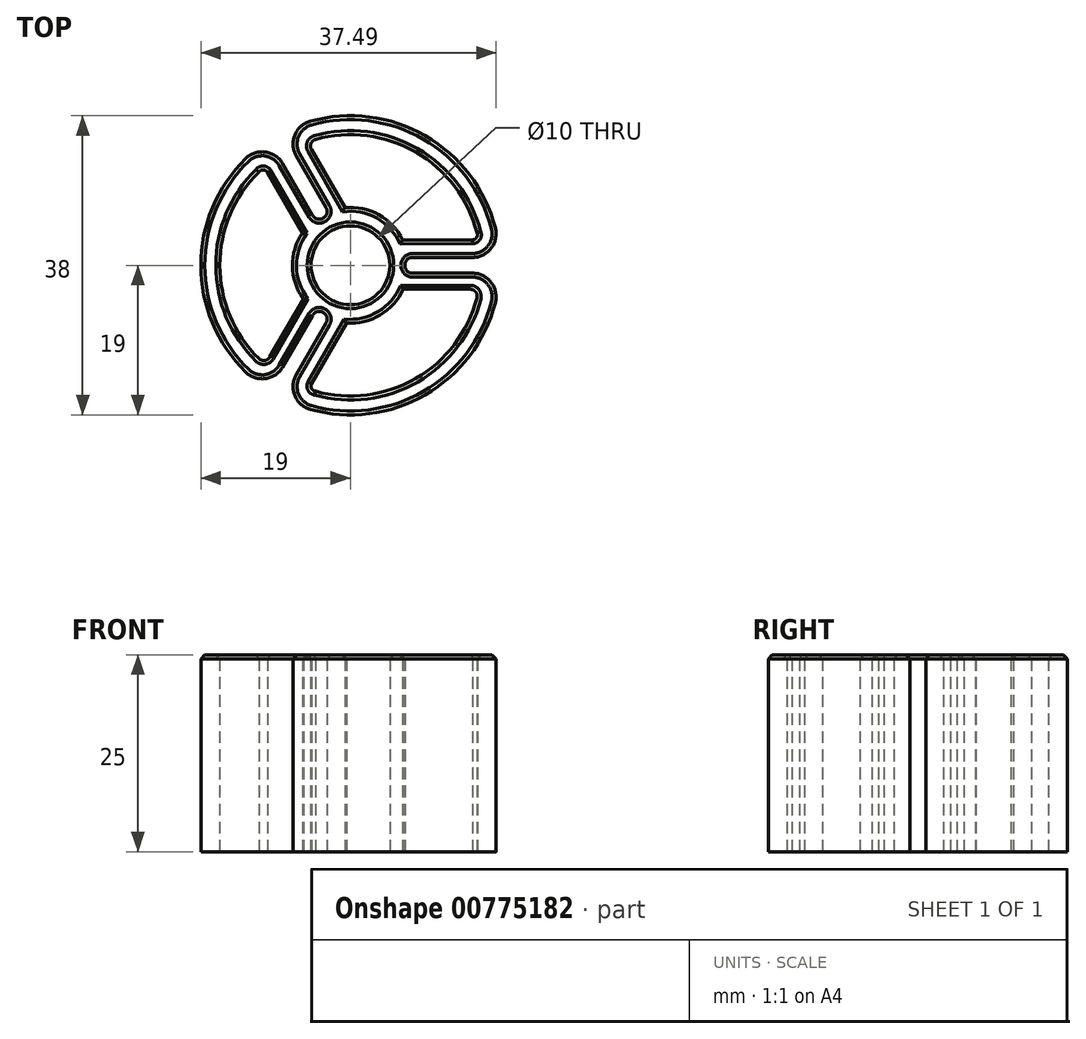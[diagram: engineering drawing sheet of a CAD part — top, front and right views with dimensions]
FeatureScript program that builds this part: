
annotation { "Feature Type Name" : "Feature", "Feature Type Description" : "" }
export const myFeature = defineFeature(function(context is Context, id is Id, definition is map)
    precondition{}
    {
        {
            var Q0;
            Q0=qCreatedBy(makeId("Top.planeOp"),FACE);
            var sketch = newSketch(context, id + "F0", { "sketchPlane" : qUnion([Q0])});
            skArc(sketch, "E0", {"start": v(-4.75, 18.4) * mm, "mid": v(-4.92, 18.35) * mm, "end": v(-5.08, 18.3) * mm});
            skArc(sketch, "E1.0", {"start": v(-4.25, 16.46) * mm, "mid": v(-4.4, 16.42) * mm, "end": v(-4.55, 16.38) * mm});
            skLineSegment(sketch, "E2", {"start": v(0, 19) * mm, "end": v(0, 40.88) * mm});
            skCircle(sketch, "E3.converted", {"center": v(0, 0) * mm, "radius": 5 * mm});
            skArc(sketch, "E4.converted", {"start": v(6.37, 2.82) * mm, "mid": v(3.4, 6.08) * mm, "end": v(-0.93, 6.9) * mm});
            skPoint(sketch, "E5.orphan", {"position": v(-3, 6.32) * mm});
            skLineSegment(sketch, "E6.3.0", {"start": v(15.5, 2.83) * mm, "end": v(10.9, 2.83) * mm});
            skArc(sketch, "E6.3.2", {"start": v(7.9, 1) * mm, "mid": v(6.9, 0) * mm, "end": v(7.9, -1) * mm});
            skLineSegment(sketch, "E6.3.3", {"start": v(12, 1) * mm, "end": v(15.5, 1) * mm});
            skLineSegment(sketch, "E6.3.4", {"start": v(15.22, -2.65) * mm, "end": v(10.83, -2.65) * mm});
            skArc(sketch, "E6.3.5", {"start": v(15.5, 1) * mm, "mid": v(17.86, 2.16) * mm, "end": v(18.4, 4.75) * mm});
            skLineSegment(sketch, "E6.3.6", {"start": v(12, -1) * mm, "end": v(15.5, -1) * mm});
            skPoint(sketch, "E6.3.7", {"position": v(16.73, 3) * mm});
            skArc(sketch, "E6.3.8", {"start": v(18.4, -4.75) * mm, "mid": v(17.86, -2.16) * mm, "end": v(15.5, -1) * mm});
            skPoint(sketch, "E6.3.9", {"position": v(16.73, -3) * mm});
            skArc(sketch, "E6.3.10", {"start": v(15.5, 2.83) * mm, "mid": v(16.35, 3.3) * mm, "end": v(16.46, 4.26) * mm});
            skArc(sketch, "E6.3.11", {"start": v(16.46, -4.25) * mm, "mid": v(16.23, -3.14) * mm, "end": v(15.22, -2.65) * mm});
            skLineSegment(sketch, "E6.3.12", {"start": v(12, 1) * mm, "end": v(7.9, 1) * mm});
            skLineSegment(sketch, "E6.3.13", {"start": v(12, -1) * mm, "end": v(7.9, -1) * mm});
            skArc(sketch, "E7.trimOffspring", {"start": v(16.46, 4.26) * mm, "mid": v(8.63, 14.65) * mm, "end": v(-4.25, 16.46) * mm});
            skArc(sketch, "E8.trimOffspring", {"start": v(18.4, 4.75) * mm, "mid": v(9.65, 16.37) * mm, "end": v(-4.75, 18.4) * mm});
            skArc(sketch, "E9.trimOffspring", {"start": v(-4.75, -18.4) * mm, "mid": v(9.65, -16.37) * mm, "end": v(18.4, -4.75) * mm});
            skArc(sketch, "E10.trimOffspring", {"start": v(-4.25, -16.46) * mm, "mid": v(8.63, -14.64) * mm, "end": v(16.46, -4.25) * mm});
            skArc(sketch, "E11.trimOffspring", {"start": v(-18.4, -4.75) * mm, "mid": v(-16.45, -9.5) * mm, "end": v(-13.31, -13.56) * mm});
            skArc(sketch, "E12.trimOffspring", {"start": v(-16.46, -4.25) * mm, "mid": v(-14.72, -8.5) * mm, "end": v(-11.91, -12.13) * mm});
            skLineSegment(sketch, "E13", {"start": v(10.9, 2.83) * mm, "end": v(6.37, 2.82) * mm});
            skLineSegment(sketch, "E14", {"start": v(10.83, -2.65) * mm, "end": v(6.44, -2.65) * mm});
            skArc(sketch, "E15.1.0", {"start": v(-8.61, 12.92) * mm, "mid": v(-10.8, 14.39) * mm, "end": v(-13.31, 13.56) * mm});
            skArc(sketch, "E15.1.1", {"start": v(-4.82, 6.35) * mm, "mid": v(-3.45, 5.98) * mm, "end": v(-3.09, 7.35) * mm});
            skArc(sketch, "E15.1.2", {"start": v(-5.08, 18.3) * mm, "mid": v(-7.06, 16.55) * mm, "end": v(-6.88, 13.92) * mm});
            skLineSegment(sketch, "E15.1.3", {"start": v(-5.32, 14.5) * mm, "end": v(-3.12, 10.7) * mm});
            skPoint(sketch, "E15.1.4", {"position": v(-10.96, 13) * mm});
            skLineSegment(sketch, "E15.1.5", {"start": v(-6.87, 9.9) * mm, "end": v(-4.82, 6.35) * mm});
            skLineSegment(sketch, "E15.1.6", {"start": v(-3.12, 10.7) * mm, "end": v(-0.93, 6.9) * mm});
            skLineSegment(sketch, "E15.1.7", {"start": v(-5.13, 10.9) * mm, "end": v(-3.09, 7.35) * mm});
            skLineSegment(sketch, "E15.1.8", {"start": v(-6.87, 9.9) * mm, "end": v(-8.61, 12.92) * mm});
            skLineSegment(sketch, "E15.1.9", {"start": v(-5.13, 10.9) * mm, "end": v(-6.88, 13.92) * mm});
            skLineSegment(sketch, "E15.1.10", {"start": v(-7.9, 8.03) * mm, "end": v(-5.63, 4.1) * mm});
            skLineSegment(sketch, "E15.1.11", {"start": v(-10.2, 12) * mm, "end": v(-7.9, 8.03) * mm});
            skPoint(sketch, "E15.1.12", {"position": v(-5.77, 16) * mm});
            skArc(sketch, "E15.1.13", {"start": v(-10.2, 12) * mm, "mid": v(-11.03, 12.5) * mm, "end": v(-11.92, 12.12) * mm});
            skArc(sketch, "E15.1.14", {"start": v(-4.55, 16.38) * mm, "mid": v(-5.4, 15.63) * mm, "end": v(-5.32, 14.5) * mm});
            skArc(sketch, "E15.2.0", {"start": v(-6.88, -13.92) * mm, "mid": v(-7.06, -16.55) * mm, "end": v(-5.08, -18.3) * mm});
            skArc(sketch, "E15.2.1", {"start": v(-3.09, -7.35) * mm, "mid": v(-3.45, -5.98) * mm, "end": v(-4.82, -6.35) * mm});
            skArc(sketch, "E15.2.2", {"start": v(-13.31, -13.56) * mm, "mid": v(-10.8, -14.39) * mm, "end": v(-8.61, -12.92) * mm});
            skLineSegment(sketch, "E15.2.3", {"start": v(-9.9, -11.86) * mm, "end": v(-7.7, -8.05) * mm});
            skPoint(sketch, "E15.2.4", {"position": v(-5.77, -16) * mm});
            skLineSegment(sketch, "E15.2.5", {"start": v(-5.13, -10.9) * mm, "end": v(-3.09, -7.35) * mm});
            skLineSegment(sketch, "E15.2.6", {"start": v(-7.7, -8.05) * mm, "end": v(-5.51, -4.25) * mm});
            skLineSegment(sketch, "E15.2.7", {"start": v(-6.87, -9.9) * mm, "end": v(-4.82, -6.35) * mm});
            skLineSegment(sketch, "E15.2.8", {"start": v(-5.13, -10.9) * mm, "end": v(-6.88, -13.92) * mm});
            skLineSegment(sketch, "E15.2.9", {"start": v(-6.87, -9.9) * mm, "end": v(-8.61, -12.92) * mm});
            skLineSegment(sketch, "E15.2.10", {"start": v(-3, -10.86) * mm, "end": v(-0.74, -6.92) * mm});
            skLineSegment(sketch, "E15.2.11", {"start": v(-5.3, -14.84) * mm, "end": v(-3, -10.86) * mm});
            skPoint(sketch, "E15.2.12", {"position": v(-10.96, -13) * mm});
            skArc(sketch, "E15.2.13", {"start": v(-5.3, -14.84) * mm, "mid": v(-5.32, -15.8) * mm, "end": v(-4.54, -16.38) * mm});
            skArc(sketch, "E15.2.14", {"start": v(-11.91, -12.13) * mm, "mid": v(-10.84, -12.49) * mm, "end": v(-9.9, -11.86) * mm});
            skArc(sketch, "E16.trimOffspring", {"start": v(-13.31, 13.56) * mm, "mid": v(-18.3, 5.08) * mm, "end": v(-18.4, -4.75) * mm});
            skArc(sketch, "E17.trimOffspring", {"start": v(-11.92, 12.12) * mm, "mid": v(-16.38, 4.54) * mm, "end": v(-16.46, -4.25) * mm});
            skArc(sketch, "E18.trimOffspring", {"start": v(-5.63, 4.1) * mm, "mid": v(-6.96, -0.1) * mm, "end": v(-5.51, -4.25) * mm});
            skArc(sketch, "E19.trimOffspring", {"start": v(-5.08, -18.3) * mm, "mid": v(-4.92, -18.35) * mm, "end": v(-4.75, -18.4) * mm});
            skArc(sketch, "E20.trimOffspring", {"start": v(-4.54, -16.38) * mm, "mid": v(-4.4, -16.42) * mm, "end": v(-4.25, -16.46) * mm});
            skArc(sketch, "E21.trimOffspring", {"start": v(-0.74, -6.92) * mm, "mid": v(3.56, -5.98) * mm, "end": v(6.44, -2.65) * mm});
            skArc(sketch, "E22.0", {"start": v(-6.1, 4.12) * mm, "mid": v(-7.36, -0.1) * mm, "end": v(-5.99, -4.28) * mm});
            skLineSegment(sketch, "E23.0", {"start": v(-8.25, 7.83) * mm, "end": v(-6.1, 4.12) * mm});
            skLineSegment(sketch, "E23.1", {"start": v(-10.55, 11.8) * mm, "end": v(-8.25, 7.83) * mm});
            skArc(sketch, "E23.2", {"start": v(-10.55, 11.8) * mm, "mid": v(-11.07, 12.11) * mm, "end": v(-11.62, 11.86) * mm});
            skArc(sketch, "E23.3", {"start": v(-11.62, 11.86) * mm, "mid": v(-16, 4.45) * mm, "end": v(-16.07, -4.15) * mm});
            skLineSegment(sketch, "E23.4", {"start": v(-7.95, -7.69) * mm, "end": v(-5.99, -4.28) * mm});
            skLineSegment(sketch, "E23.5", {"start": v(-10.25, -11.66) * mm, "end": v(-7.95, -7.69) * mm});
            skArc(sketch, "E23.6", {"start": v(-11.63, -11.84) * mm, "mid": v(-10.9, -12.09) * mm, "end": v(-10.25, -11.66) * mm});
            skArc(sketch, "E23.7", {"start": v(-16.07, -4.15) * mm, "mid": v(-14.38, -8.3) * mm, "end": v(-11.63, -11.84) * mm});
            skArc(sketch, "E24.1.0", {"start": v(-0.52, -7.34) * mm, "mid": v(3.76, -6.33) * mm, "end": v(6.7, -3.05) * mm});
            skLineSegment(sketch, "E24.1.1", {"start": v(-2.66, -11.06) * mm, "end": v(-0.52, -7.34) * mm});
            skLineSegment(sketch, "E24.1.2", {"start": v(-4.95, -15.03) * mm, "end": v(-2.66, -11.06) * mm});
            skArc(sketch, "E24.1.3", {"start": v(-4.95, -15.03) * mm, "mid": v(-4.95, -15.64) * mm, "end": v(-4.46, -16) * mm});
            skArc(sketch, "E24.1.4", {"start": v(-4.46, -16) * mm, "mid": v(4.14, -16.07) * mm, "end": v(11.63, -11.84) * mm});
            skArc(sketch, "E24.1.5", {"start": v(11.63, -11.84) * mm, "mid": v(14.38, -8.3) * mm, "end": v(16.07, -4.15) * mm});
            skArc(sketch, "E24.1.6", {"start": v(16.07, -4.15) * mm, "mid": v(15.92, -3.39) * mm, "end": v(15.22, -3.05) * mm});
            skLineSegment(sketch, "E24.1.7", {"start": v(15.22, -3.05) * mm, "end": v(10.63, -3.05) * mm});
            skLineSegment(sketch, "E24.1.8", {"start": v(10.63, -3.05) * mm, "end": v(6.7, -3.05) * mm});
            skArc(sketch, "E24.2.0", {"start": v(6.62, 3.22) * mm, "mid": v(3.6, 6.42) * mm, "end": v(-0.71, 7.33) * mm});
            skLineSegment(sketch, "E24.2.1", {"start": v(10.9, 3.23) * mm, "end": v(6.62, 3.22) * mm});
            skLineSegment(sketch, "E24.2.2", {"start": v(15.5, 3.23) * mm, "end": v(10.9, 3.23) * mm});
            skArc(sketch, "E24.2.3", {"start": v(15.5, 3.23) * mm, "mid": v(16.02, 3.53) * mm, "end": v(16.08, 4.13) * mm});
            skArc(sketch, "E24.2.4", {"start": v(16.08, 4.13) * mm, "mid": v(11.85, 11.62) * mm, "end": v(4.44, 16) * mm});
            skArc(sketch, "E24.2.5", {"start": v(4.44, 16) * mm, "mid": v(0, 16.6) * mm, "end": v(-4.44, 16) * mm});
            skArc(sketch, "E24.2.6", {"start": v(-4.44, 16) * mm, "mid": v(-5.02, 15.48) * mm, "end": v(-4.97, 14.7) * mm});
            skLineSegment(sketch, "E24.2.7", {"start": v(-4.97, 14.7) * mm, "end": v(-2.68, 10.73) * mm});
            skLineSegment(sketch, "E24.2.8", {"start": v(-2.68, 10.73) * mm, "end": v(-0.71, 7.33) * mm});
            skSolve(sketch);
        }
        {
            var Q0;
            {var subQ1=sQuery(id+"F0.wireOp",EDGE,"E0");Q0=makeQuery(id+"F0.imprint","IMPRINT",FACE,{"disambiguationData":[TD([[makeQuery(id+"F0.imprint","IMPRINT",EDGE,{"derivedFrom":subQ1}),1.0]])]});}
            var Q1;
            Q1=makeQuery(id+"F0.imprint","IMPRINT",FACE,{"disambiguationData":[TD([[makeQuery(id+"F0.imprint","IMPRINT",EDGE,{"derivedFrom":sQuery(id+"F0.wireOp",EDGE,"E12.trimOffspring")}),1.0]])]});
            var Q2;
            Q2=makeQuery(id+"F0.imprint","IMPRINT",FACE,{"disambiguationData":[TD([[makeQuery(id+"F0.imprint","IMPRINT",EDGE,{"derivedFrom":sQuery(id+"F0.wireOp",EDGE,"E6.3.4")}),1.0]])]});
            var Q3;
            Q3=makeQuery(id+"F0.imprint","IMPRINT",FACE,{"disambiguationData":[TD([[makeQuery(id+"F0.imprint","IMPRINT",EDGE,{"derivedFrom":sQuery(id+"F0.wireOp",EDGE,"E1.0")}),1.0]])]});
            extrude(context, id + "F1", {"entities" : qUnion([Q0, Q1, Q2, Q3]), "depth" : 25 * mm, "offsetDistance" : 25 * mm});
        }
        {
            var Q0;
            Q0=makeQuery(id+"F1.opExtrude","CAP_FACE",FACE,{"disambiguationData":[OSD([sQuery(id+"F0.wireOp",EDGE,"E0"),sQuery(id+"F0.wireOp",EDGE,"E3.converted"),sQuery(id+"F0.wireOp",EDGE,"E6.3.2"),sQuery(id+"F0.wireOp",EDGE,"E6.3.3"),sQuery(id+"F0.wireOp",EDGE,"E6.3.5"),sQuery(id+"F0.wireOp",EDGE,"E6.3.6"),sQuery(id+"F0.wireOp",EDGE,"E6.3.8"),sQuery(id+"F0.wireOp",EDGE,"E6.3.12"),sQuery(id+"F0.wireOp",EDGE,"E6.3.13"),sQuery(id+"F0.wireOp",EDGE,"E8.trimOffspring"),sQuery(id+"F0.wireOp",EDGE,"E9.trimOffspring"),sQuery(id+"F0.wireOp",EDGE,"E11.trimOffspring"),sQuery(id+"F0.wireOp",EDGE,"E15.1.0"),sQuery(id+"F0.wireOp",EDGE,"E15.1.1"),sQuery(id+"F0.wireOp",EDGE,"E15.1.2"),sQuery(id+"F0.wireOp",EDGE,"E15.1.5"),sQuery(id+"F0.wireOp",EDGE,"E15.1.7"),sQuery(id+"F0.wireOp",EDGE,"E15.1.8"),sQuery(id+"F0.wireOp",EDGE,"E15.1.9"),sQuery(id+"F0.wireOp",EDGE,"E15.2.0"),sQuery(id+"F0.wireOp",EDGE,"E15.2.1"),sQuery(id+"F0.wireOp",EDGE,"E15.2.2"),sQuery(id+"F0.wireOp",EDGE,"E15.2.5"),sQuery(id+"F0.wireOp",EDGE,"E15.2.7"),sQuery(id+"F0.wireOp",EDGE,"E15.2.8"),sQuery(id+"F0.wireOp",EDGE,"E15.2.9"),sQuery(id+"F0.wireOp",EDGE,"E16.trimOffspring"),sQuery(id+"F0.wireOp",EDGE,"E19.trimOffspring"),sQuery(id+"F0.wireOp",EDGE,"E22.0"),sQuery(id+"F0.wireOp",EDGE,"E23.0"),sQuery(id+"F0.wireOp",EDGE,"E23.1"),sQuery(id+"F0.wireOp",EDGE,"E23.2"),sQuery(id+"F0.wireOp",EDGE,"E23.3"),sQuery(id+"F0.wireOp",EDGE,"E23.4"),sQuery(id+"F0.wireOp",EDGE,"E23.5"),sQuery(id+"F0.wireOp",EDGE,"E23.6"),sQuery(id+"F0.wireOp",EDGE,"E23.7"),sQuery(id+"F0.wireOp",EDGE,"E24.1.0"),sQuery(id+"F0.wireOp",EDGE,"E24.1.1"),sQuery(id+"F0.wireOp",EDGE,"E24.1.2"),sQuery(id+"F0.wireOp",EDGE,"E24.1.3"),sQuery(id+"F0.wireOp",EDGE,"E24.1.4"),sQuery(id+"F0.wireOp",EDGE,"E24.1.5"),sQuery(id+"F0.wireOp",EDGE,"E24.1.6"),sQuery(id+"F0.wireOp",EDGE,"E24.1.7"),sQuery(id+"F0.wireOp",EDGE,"E24.1.8"),sQuery(id+"F0.wireOp",EDGE,"E24.2.0"),sQuery(id+"F0.wireOp",EDGE,"E24.2.1"),sQuery(id+"F0.wireOp",EDGE,"E24.2.2"),sQuery(id+"F0.wireOp",EDGE,"E24.2.3"),sQuery(id+"F0.wireOp",EDGE,"E24.2.4"),sQuery(id+"F0.wireOp",EDGE,"E24.2.5"),sQuery(id+"F0.wireOp",EDGE,"E24.2.6"),sQuery(id+"F0.wireOp",EDGE,"E24.2.7"),sQuery(id+"F0.wireOp",EDGE,"E24.2.8")])],"isStart":false});
            chamfer(context, id + "F2", {"entities" : qUnion([Q0]), "width" : .5 * mm, "tangentPropagation" : true});
        }
    });
